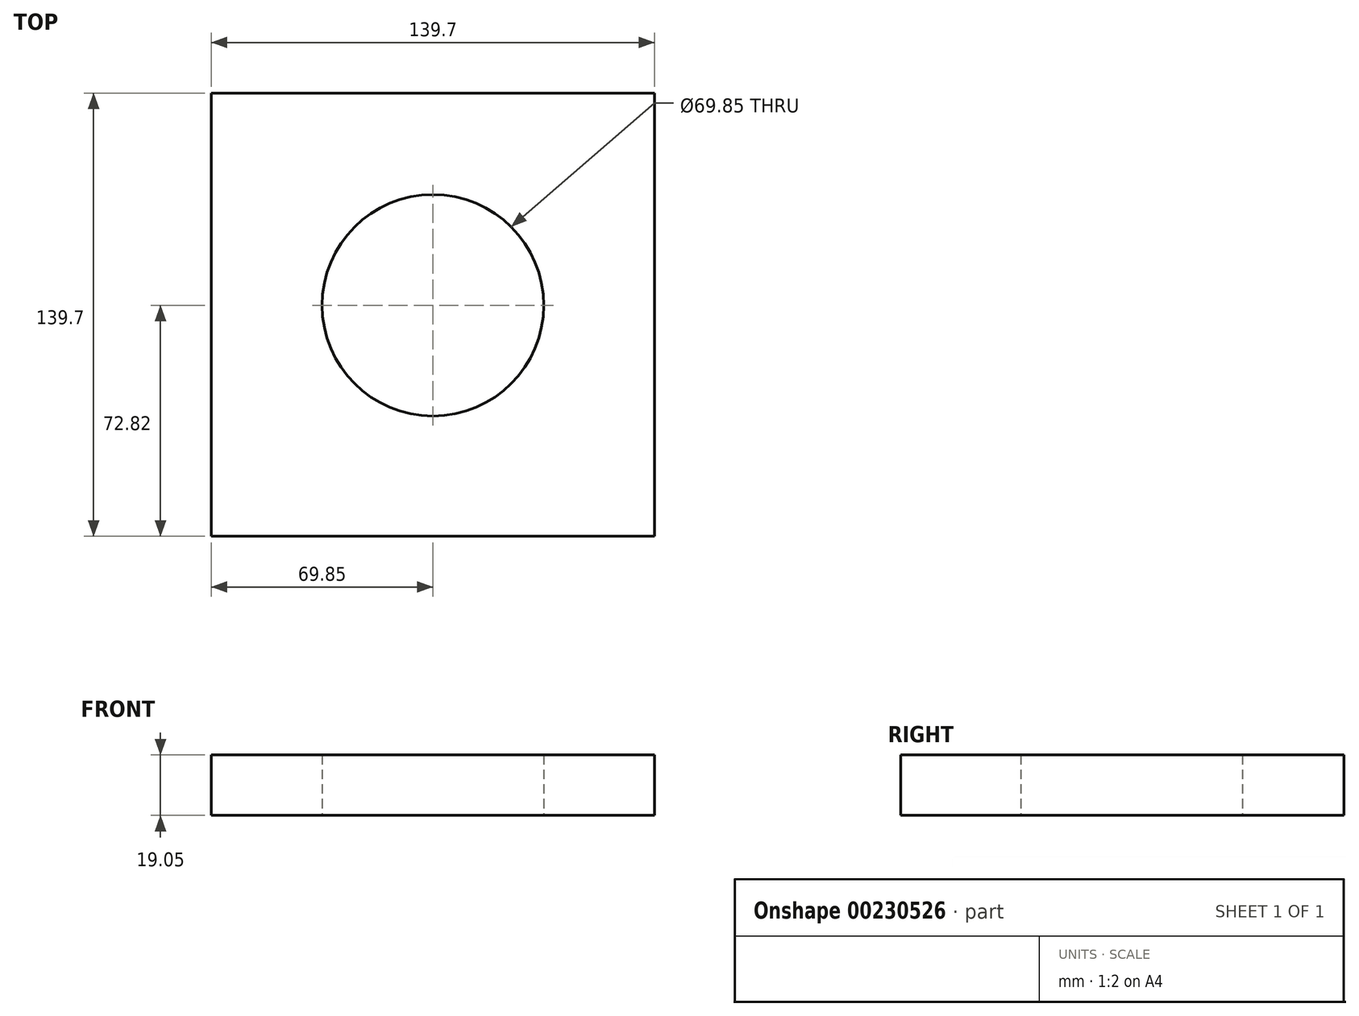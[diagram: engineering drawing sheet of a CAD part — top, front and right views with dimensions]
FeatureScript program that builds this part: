
annotation { "Feature Type Name" : "Feature", "Feature Type Description" : "" }
export const myFeature = defineFeature(function(context is Context, id is Id, definition is map)
    precondition{}
    {
        {
            var Q0;
            Q0=qCreatedBy(makeId("Top.planeOp"),FACE);
            var sketch = newSketch(context, id + "F0", { "sketchPlane" : qUnion([Q0])});
            skLineSegment(sketch, "E0.bottom", {"start": v(-69.85, 66.88) * mm, "end": v(69.85, 66.88) * mm});
            skLineSegment(sketch, "E0.top", {"start": v(-69.85, -72.82) * mm, "end": v(69.85, -72.82) * mm});
            skLineSegment(sketch, "E0.left", {"start": v(-69.85, 66.88) * mm, "end": v(-69.85, -72.82) * mm});
            skLineSegment(sketch, "E0.right", {"start": v(69.85, 66.88) * mm, "end": v(69.85, -72.82) * mm});
            skPoint(sketch, "E0.middle", {"position": v(0, -2.97) * mm});
            skCircle(sketch, "E1", {"center": v(0, 0) * mm, "radius": 34.93 * mm});
            skSolve(sketch);
        }
        {
            var Q0;
            Q0 = qSketchRegion(id + "F0", true);
            extrude(context, id + "F1", {"entities" : qUnion([Q0]), "depth" : 19.05 * mm});
        }
    });
